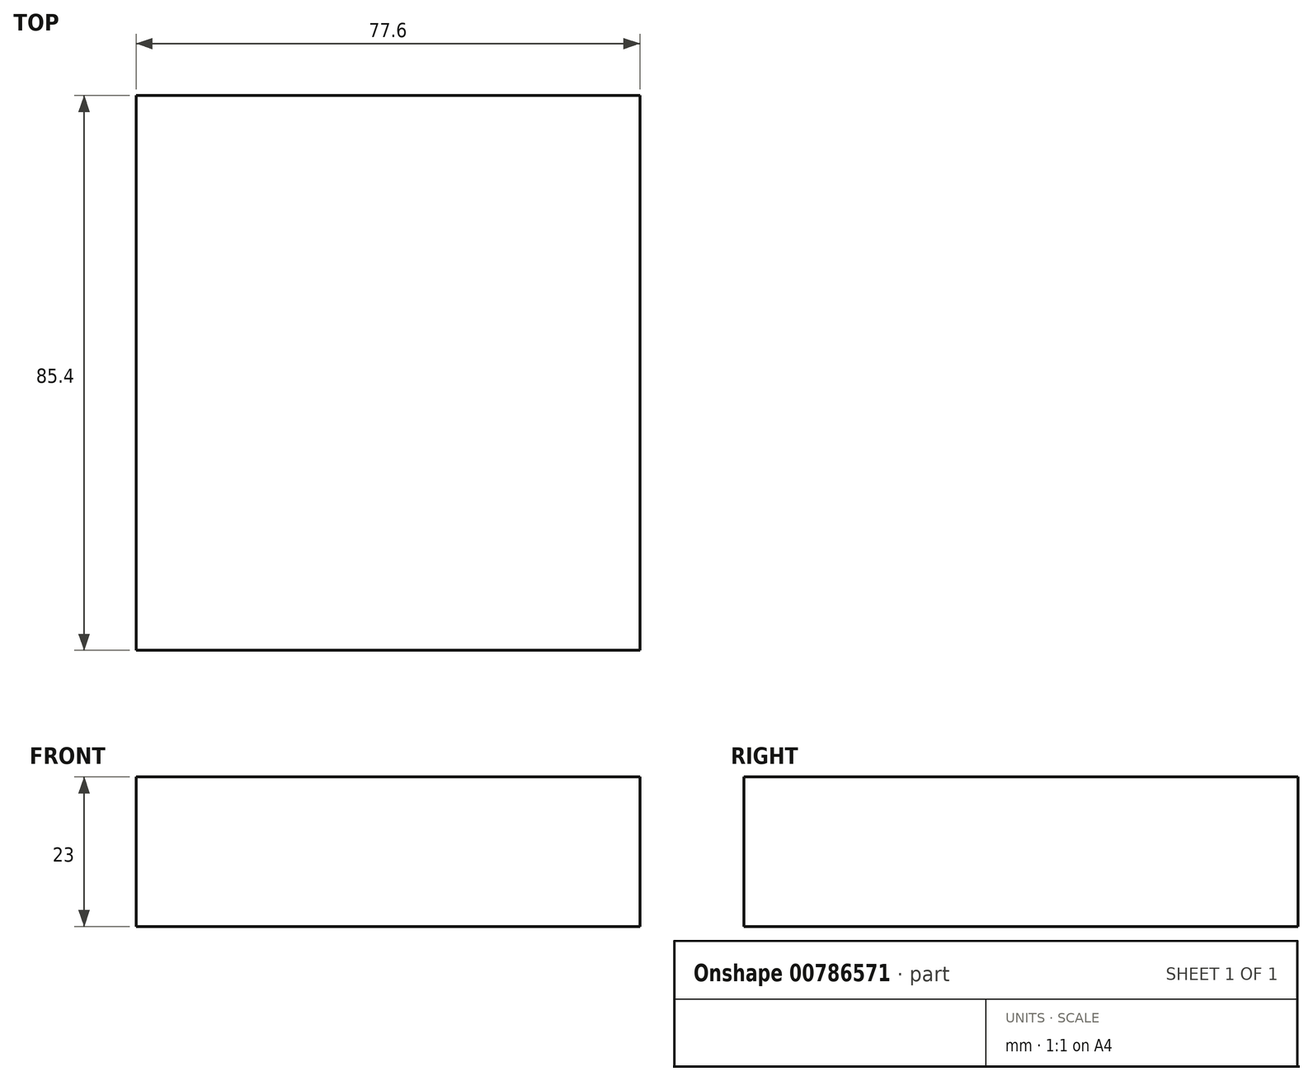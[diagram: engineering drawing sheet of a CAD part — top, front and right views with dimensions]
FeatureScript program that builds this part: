
annotation { "Feature Type Name" : "Feature", "Feature Type Description" : "" }
export const myFeature = defineFeature(function(context is Context, id is Id, definition is map)
    precondition{}
    {
        {
            var Q0;
            Q0=qCreatedBy(makeId("Top.planeOp"),FACE);
            var sketch = newSketch(context, id + "F0", { "sketchPlane" : qUnion([Q0])});
            skLineSegment(sketch, "E0.bottom", {"start": v(-70.96, 0) * mm, "end": v(6.64, 0) * mm});
            skLineSegment(sketch, "E0.top", {"start": v(-70.96, 85.4) * mm, "end": v(6.64, 85.4) * mm});
            skLineSegment(sketch, "E0.left", {"start": v(-70.96, 0) * mm, "end": v(-70.96, 85.4) * mm});
            skLineSegment(sketch, "E0.right", {"start": v(6.64, 0) * mm, "end": v(6.64, 85.4) * mm});
            skSolve(sketch);
        }
        {
            var Q0;
            Q0 = qSketchRegion(id + "F0", true);
            extrude(context, id + "F1", {"entities" : qUnion([Q0]), "depth" : 23 * mm, "offsetDistance" : 25.4 * mm});
        }
    });
